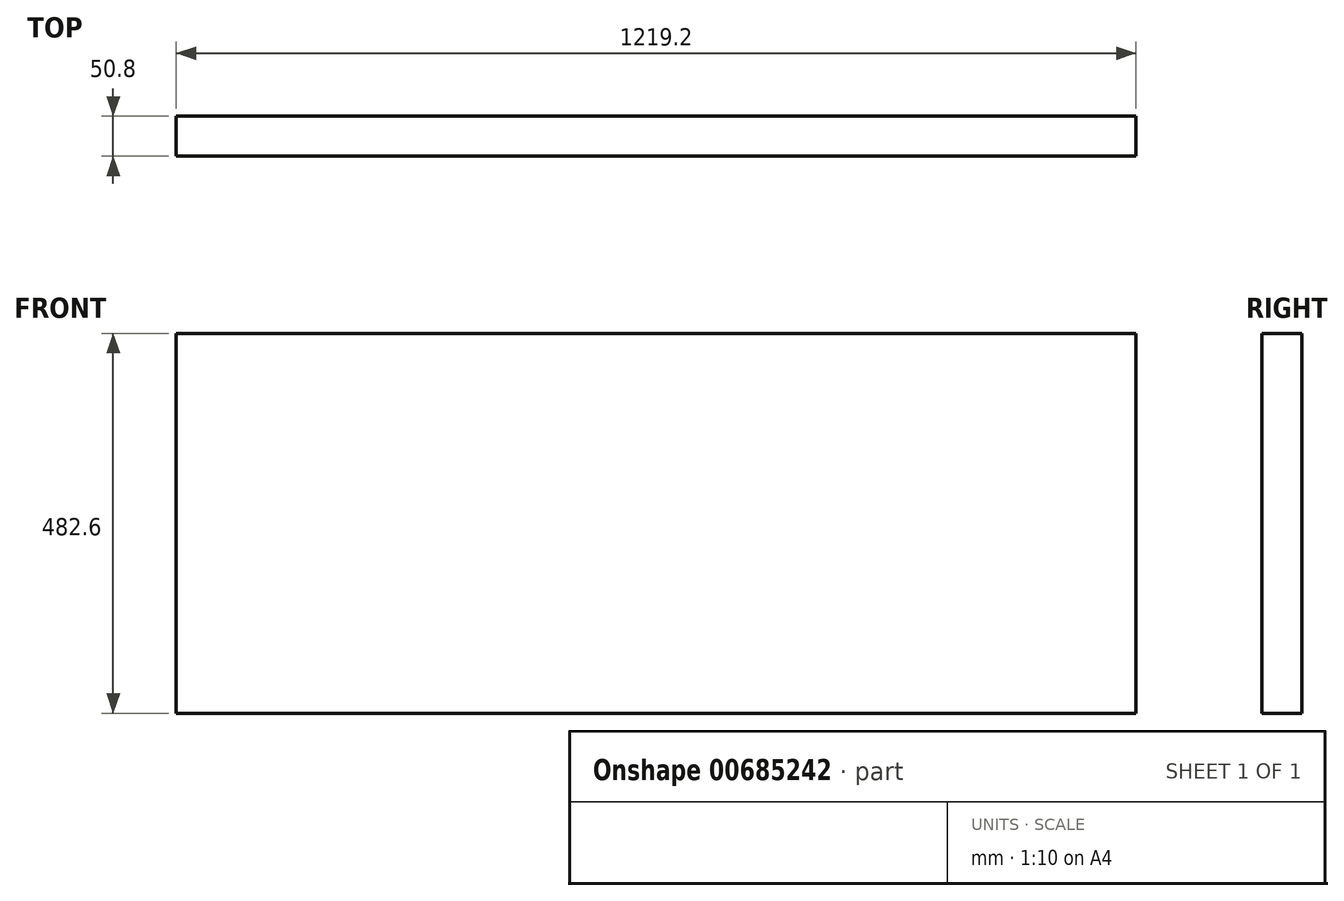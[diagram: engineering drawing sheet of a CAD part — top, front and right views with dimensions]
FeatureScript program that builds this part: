
annotation { "Feature Type Name" : "Feature", "Feature Type Description" : "" }
export const myFeature = defineFeature(function(context is Context, id is Id, definition is map)
    precondition{}
    {
        {
            var Q0;
            Q0=qCreatedBy(makeId("Top.planeOp"),FACE);
            var sketch = newSketch(context, id + "F0", { "sketchPlane" : qUnion([Q0])});
            skLineSegment(sketch, "E0.bottom", {"start": v(609.6, 25.4) * mm, "end": v(-609.6, 25.4) * mm});
            skLineSegment(sketch, "E0.top", {"start": v(609.6, -25.4) * mm, "end": v(-609.6, -25.4) * mm});
            skLineSegment(sketch, "E0.left", {"start": v(609.6, 25.4) * mm, "end": v(609.6, -25.4) * mm});
            skLineSegment(sketch, "E0.right", {"start": v(-609.6, 25.4) * mm, "end": v(-609.6, -25.4) * mm});
            skPoint(sketch, "E0.middle", {"position": v(0, 0) * mm});
            skSolve(sketch);
        }
        {
            var Q0;
            Q0 = qSketchRegion(id + "F0", true);
            extrude(context, id + "F1", {"entities" : qUnion([Q0]), "depth" : 482.6 * mm, "offsetDistance" : 25.4 * mm});
        }
    });
